# Revit family: Hand_Dryer-Excel_Dryer-XLERATOR_Unit
name_source: partatom
category: Specialty Equipment
revit_build: Autodesk Revit Architecture 2013 (Build: 20130531_2115(x64)
units: mm (PartAtom-declared; Revit-internal decimal feet)

## types (25) — shared parameters
ADA Compliance = http://www.exceldryer.com
Air Temperature (Farenheit) = 135 °F
Apparent Load = 1500 VA
Assembly Code = C1030200
Category = Toilet Accessories
Cost Information = http://www.exceldryer.com
Cost Savings Analysis = http://www.exceldryer.com
Default Elevation = 3' - 5"
Depth = 0' - 6 7/8"
Description = XLERATOR Hand Dryer
Dry Time = 10-15 Seconds
Expected Lifespan = 15+ Years
Green Building LEED = http://www.exceldryer.com
Heating Element = 900 Watts
Height = 1' - 0 7/8"
Impact Resistant Note = UL 499
Installation Phase = Single
Installation URL = http://www.exceldryer.com
Maintenance Schedule = Once to Twice per Year
Maintenance URL = http://www.exceldryer.com
Manufacturer = Excel Dryer
Manufacturer Fax = 1-413-525-2853
Manufacturer Toll Free Number = 800-255-9235
Motor Note = 12.5 A@110/120V Single phase (4.5A eco); 7.0 A @208V Single phase (2.1A eco); 6.5 A @220/240V Single phase(2.2A eco); 5.5 A @277V Single phase (no eco available).
Mounting Note = For correct placement, match Elevation to Mounting Height.
Noise Reduction Nozzle Product Documentation Link = http://www.exceldryer.com
Number of Poles = 1
Output at Outlet (LFM) = 16000
Phase = 1
Power Factor = 1
Product Documentation Link = http://www.exceldryer.com
Product Name = XLERATOR Hand Dryer
Product Page URL = http://www.exceldryer.com
Run-Time Cycle = Automatic
Subcategory = Hand Dryers
Time Cycle = Automatic
URL = http://www.exceldryer.com
Void = 0' - 0 1/16"
Void Depth = 7' - 5 15/16"
Warranty Duration = 5 Years
Watts = 15000 W
Width = 0' - 11 15/16"
ecoScorecard Product Page = http://exceldryer.ecoscorecard.com

## per-type parameters (varying)
| type | Amperage | Cover Finish | Cover Material | Frequency | Model | Product Weight | Voltage |
| XL-BW-120V | 13 A | Bulk Molding Compound -  Excel Dryer - Thermoset Resin - White | Thermoset Resin | 60 Hz | XL-BW | 15lbs | 120 V |
| XL-BW-208V | 7 A | Bulk Molding Compound -  Excel Dryer - Thermoset Resin - White | Thermoset Resin | 60 Hz | XL-BW | 15lbs | 208 V |
| XL-BW-240V | 7 A | Bulk Molding Compound -  Excel Dryer - Thermoset Resin - White | Thermoset Resin | 60 Hz | XL-BW | 15lbs | 240 V |
| XL-BW-277V | 6 A | Bulk Molding Compound -  Excel Dryer - Thermoset Resin - White | Thermoset Resin | 60 Hz | XL-BW | 15lbs | 277 V |
| XL-BW-230V | 7 A | Bulk Molding Compound -  Excel Dryer - Thermoset Resin - White | Thermoset Resin | 50 Hz | XL-BW | 15lbs | 230 V |
| XL-SB-120V | 13 A | Metal - Excel Dryer - Stainless Steel - Brushed | Stainless Steel | 60 Hz | XL-SB | 16lbs | 120 V |
| XL-SB-208V | 7 A | Metal - Excel Dryer - Stainless Steel - Brushed | Stainless Steel | 60 Hz | XL-SB | 16lbs | 208 V |
| XL-SB-240V | 7 A | Metal - Excel Dryer - Stainless Steel - Brushed | Stainless Steel | 60 Hz | XL-SB | 16lbs | 240 V |
| XL-SB-277V | 6 A | Metal - Excel Dryer - Stainless Steel - Brushed | Stainless Steel | 60 Hz | XL-SB | 16lbs | 277 V |
| XL-SB-230V | 7 A | Metal - Excel Dryer - Stainless Steel - Brushed | Stainless Steel | 50 Hz | XL-SB | 16lbs | 230 V |
| XL-C-120V | 13 A | Metal - Excel Dryer - Chrome - Polished | Stainless Steel | 60 Hz | XL-C | 17lbs | 120 V |
| XL-C-208V | 7 A | Metal - Excel Dryer - Chrome - Polished | Stainless Steel | 60 Hz | XL-C | 17lbs | 208 V |
| XL-C-240V | 7 A | Metal - Excel Dryer - Chrome - Polished | Stainless Steel | 60 Hz | XL-C | 17lbs | 240 V |
| XL-C-277V | 6 A | Metal - Excel Dryer - Chrome - Polished | Stainless Steel | 60 Hz | XL-C | 17lbs | 277 V |
| XL-C-230V | 7 A | Metal - Excel Dryer - Chrome - Polished | Stainless Steel | 50 Hz | XL-C | 17lbs | 230 V |
| XL-W-120V | 13 A | Metal -  Excel Dryer - Zinc Alloy - White | Die-Cast Zinc Alloy | 60 Hz | XL-W | 17lbs | 120 V |
| XL-W-208V | 7 A | Metal -  Excel Dryer - Zinc Alloy - White | Die-Cast Zinc Alloy | 60 Hz | XL-W | 17lbs | 208 V |
| XL-W-240V | 7 A | Metal -  Excel Dryer - Zinc Alloy - White | Die-Cast Zinc Alloy | 60 Hz | XL-W | 17lbs | 240 V |
| XL-W-277V | 6 A | Metal -  Excel Dryer - Zinc Alloy - White | Die-Cast Zinc Alloy | 60 Hz | XL-W | 17lbs | 277 V |
| XL-W-230V | 7 A | Metal -  Excel Dryer - Zinc Alloy - White | Die-Cast Zinc Alloy | 50 Hz | XL-W | 17lbs | 230 V |
| XL-GR-120V | 13 A | Metal - Excel Dryer - Zink Alloy -  Textured Graphite | Die-Cast Zinc Alloy | 60 Hz | XL-GR | 17lbs | 120 V |
| XL-GR-208V | 7 A | Metal - Excel Dryer - Zink Alloy -  Textured Graphite | Die-Cast Zinc Alloy | 60 Hz | XL-GR | 17lbs | 208 V |
| XL-GR-240V | 7 A | Metal - Excel Dryer - Zink Alloy -  Textured Graphite | Die-Cast Zinc Alloy | 60 Hz | XL-GR | 17lbs | 240 V |
| XL-GR-277V | 6 A | Metal - Excel Dryer - Zink Alloy -  Textured Graphite | Die-Cast Zinc Alloy | 60 Hz | XL-GR | 17lbs | 277 V |
| XL-GR-230V | 7 A | Metal - Excel Dryer - Zink Alloy -  Textured Graphite | Die-Cast Zinc Alloy | 50 Hz | XL-GR | 17lbs | 230 V |

## geometry (parser evidence)
native form markers: Blend x8, Sweep x1
no freeform markers — native parametric forms only
